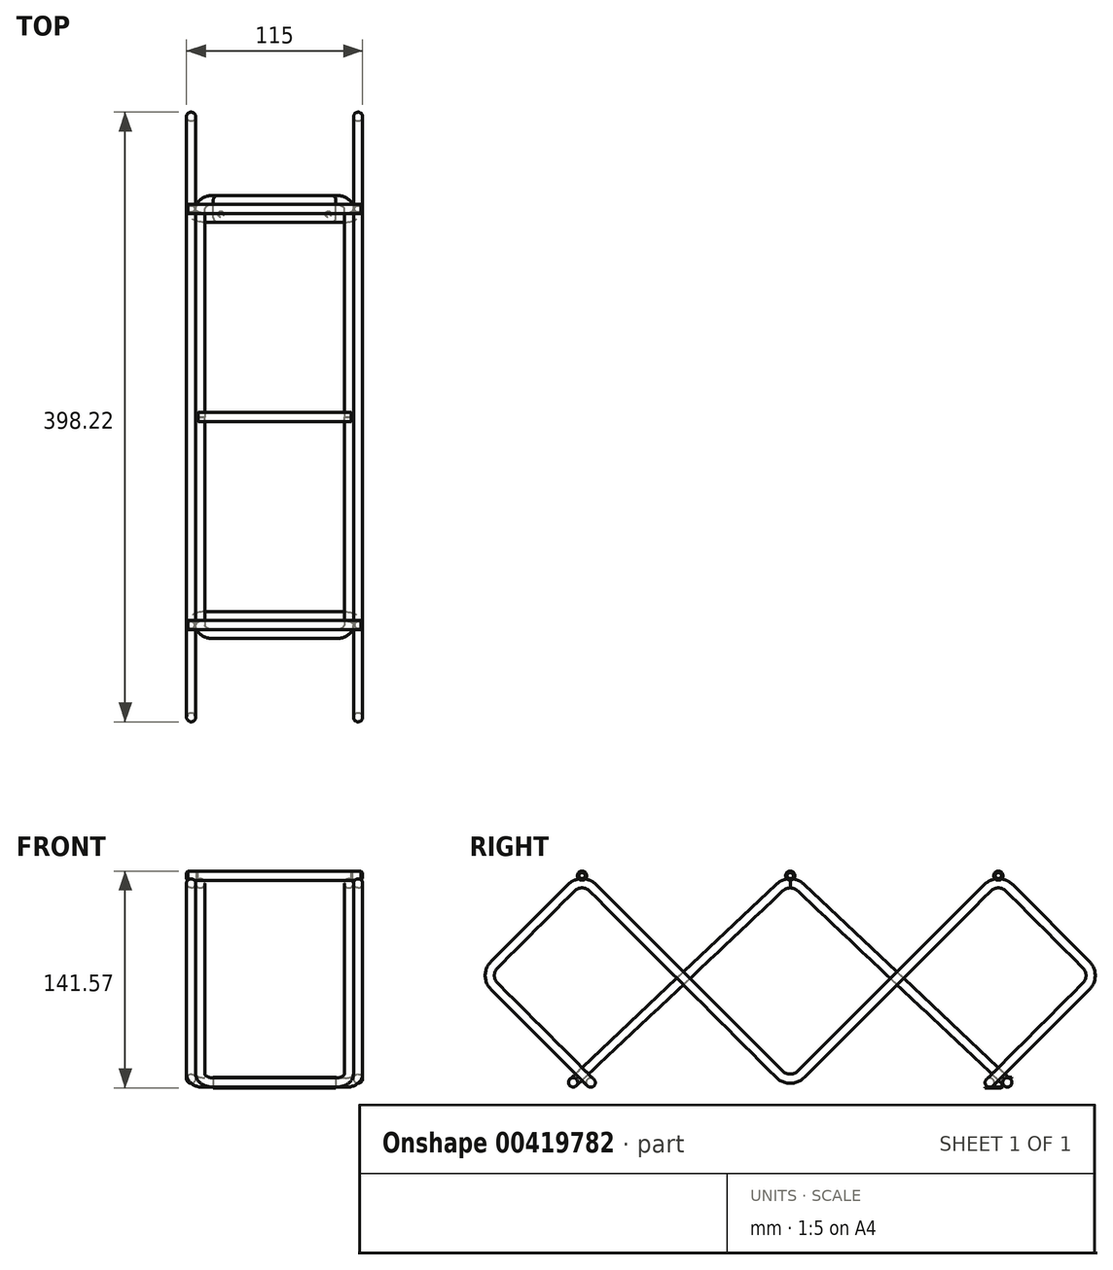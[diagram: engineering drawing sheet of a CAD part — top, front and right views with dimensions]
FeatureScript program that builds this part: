
annotation { "Feature Type Name" : "Feature", "Feature Type Description" : "" }
export const myFeature = defineFeature(function(context is Context, id is Id, definition is map)
    precondition{}
    {
        {
            var Q0;
            Q0=qCreatedBy(makeId("Right.planeOp"),FACE);
            cPlane(context, id + "F0", {"entities" : qUnion([Q0]), "cplaneType" : CPlaneType.OFFSET, "offset" : (109 / 2) * mm, "width" : 150 * mm, "height" : 150 * mm});
        }
        {
            var Q0;
            Q0=qCreatedBy(id+"F0.planeOp",FACE);
            var sketch = newSketch(context, id + "F1", { "sketchPlane" : qUnion([Q0])});
            skLineSegment(sketch, "E0", {"start": v(-7.07, 6.93) * mm, "end": v(-128.84, 128.7) * mm});
            skLineSegment(sketch, "E1", {"start": v(-142.98, 128.7) * mm, "end": v(-193.18, 78.49) * mm});
            skLineSegment(sketch, "E2", {"start": v(-193.18, 64.35) * mm, "end": v(-135.9, 7.07) * mm});
            skLineSegment(sketch, "E3", {"start": v(-135.9, 7.07) * mm, "end": v(-128.84, 0) * mm, "construction": true});
            skPoint(sketch, "E4.visualSharp", {"position": v(-135.9, 135.76) * mm});
            skArc(sketch, "E4.filletArc", {"start": v(-128.84, 128.7) * mm, "mid": v(-135.9, 131.62) * mm, "end": v(-142.98, 128.7) * mm});
            skPoint(sketch, "E5.visualSharp", {"position": v(-200.25, 71.42) * mm});
            skArc(sketch, "E5.filletArc", {"start": v(-193.18, 78.49) * mm, "mid": v(-196.11, 71.42) * mm, "end": v(-193.18, 64.35) * mm});
            skLineSegment(sketch, "E6", {"start": v(-193.18, 64.35) * mm, "end": v(-200.25, 71.42) * mm, "construction": true});
            skLineSegment(sketch, "E7", {"start": v(-128.84, 128.7) * mm, "end": v(-128.84, 0) * mm, "construction": true});
            skLineSegment(sketch, "E8", {"start": v(-128.84, 4) * mm, "end": v(0, 4) * mm, "construction": true});
            skArc(sketch, "E9", {"start": v(-7.07, 6.93) * mm, "mid": v(-3.83, 4.76) * mm, "end": v(0, 4) * mm});
            skLineSegment(sketch, "E10", {"start": v(0, 4) * mm, "end": v(7.54, 4) * mm, "construction": true});
            skLineSegment(sketch, "E11", {"start": v(-135.9, 121.62) * mm, "end": v(-135.9, 7.07) * mm, "construction": true});
            skSolve(sketch);
        }
        {
            var Q0;
            Q0=qCreatedBy(makeId("Front.planeOp"),FACE);
            var sketch = newSketch(context, id + "F2", { "sketchPlane" : qUnion([Q0])});
            skCircle(sketch, "E12", {"center": v(54.5, 4) * mm, "radius": 3 * mm});
            skSolve(sketch);
        }
        {
            var Q0;
            Q0=makeQuery(id+"F2.imprint","IMPRINT",FACE,{"disambiguationData":[TD([[makeQuery(id+"F2.imprint","IMPRINT",EDGE,{"derivedFrom":sQuery(id+"F2.wireOp",EDGE,"E12")}),1.0]])]});
            var Q1;
            Q1=sQuery(id+"F1.wireOp",EDGE,"E9");
            var Q2;
            Q2=sQuery(id+"F1.wireOp",EDGE,"E0");
            var Q3;
            Q3=sQuery(id+"F1.wireOp",EDGE,"E4.filletArc");
            var Q4;
            Q4=sQuery(id+"F1.wireOp",EDGE,"E1");
            var Q5;
            Q5=sQuery(id+"F1.wireOp",EDGE,"E5.filletArc");
            var Q6;
            Q6=sQuery(id+"F1.wireOp",EDGE,"E2");
            sweep(context, id + "F3", {"profiles" : qUnion([Q0]), "path" : qUnion([Q1, Q2, Q3, Q4, Q5, Q6])});
        }
        {
            var Q0;
            Q0=sQuery(id+"F1.wireOp",EDGE,"E3");
            var Q1;
            Q1=qCreatedBy(makeId("Right.planeOp"),FACE);
            cPlane(context, id + "F4", {"entities" : qUnion([Q0, Q1]), "cplaneType" : CPlaneType.LINE_ANGLE, "offset" : 25 * mm, "angle" : 90 * degree, "width" : 150 * mm, "height" : 150 * mm});
        }
        {
            var Q0;
            Q0=qCreatedBy(id+"F4.planeOp",FACE);
            var sketch = newSketch(context, id + "F5", { "sketchPlane" : qUnion([Q0])});
            skArc(sketch, "E13", {"start": v(-54.5, 101.1) * mm, "mid": v(-52.16, 95.44) * mm, "end": v(-46.5, 93.1) * mm});
            skLineSegment(sketch, "E14", {"start": v(-52.5, 93.1) * mm, "end": v(-46.5, 93.1) * mm, "construction": true});
            skLineSegment(sketch, "E15.0", {"start": v(-54.5, 182.1) * mm, "end": v(-54.5, 101.1) * mm, "construction": true});
            skLineSegment(sketch, "E16", {"start": v(-46.5, 93.1) * mm, "end": v(-46.5, 101.1) * mm, "construction": true});
            skLineSegment(sketch, "E17", {"start": v(-54.5, 101.1) * mm, "end": v(-46.5, 101.1) * mm, "construction": true});
            skLineSegment(sketch, "E18", {"start": v(-46.5, 93.1) * mm, "end": v(0, 93.1) * mm});
            skSolve(sketch);
        }
        {
            var Q0;
            Q0=makeQuery(id+"F3.opSweep","CAP_FACE",FACE,{"disambiguationData":[OSD([sQuery(id+"F1.wireOp",VERTEX,"E2.end"),sQuery(id+"F2.wireOp",EDGE,"E12")])],"isStart":false});
            var Q1;
            Q1=sQuery(id+"F5.wireOp",EDGE,"E13");
            var Q2;
            Q2=sQuery(id+"F5.wireOp",EDGE,"E18");
            sweep(context, id + "F6", {"operationType" : NewBodyOperationType.ADD, "profiles" : qUnion([Q0]), "path" : qUnion([Q1, Q2])});
        }
        {
            var Q0;
            Q0=makeQuery(id+"F3.opSweep","SWEPT_BODY",BODY,{"disambiguationData":[OSD([sQuery(id+"F1.wireOp",EDGE,"E2"),sQuery(id+"F2.wireOp",EDGE,"E12")])]});
            var Q1;
            Q1=makeQuery(id+"F6.opSweep","CAP_FACE",FACE,{"disambiguationData":[OSD([sQuery(id+"F1.wireOp",VERTEX,"E2.end"),sQuery(id+"F2.wireOp",EDGE,"E12"),sQuery(id+"F5.wireOp",VERTEX,"E18.end")])],"isStart":false});
            mirror(context, id + "F7", {"operationType" : NewBodyOperationType.ADD, "entities" : qUnion([Q0]), "mirrorPlane" : qUnion([Q1])});
        }
        {
            var Q0;
            Q0=qCreatedBy(makeId("Right.planeOp"),FACE);
            var sketch = newSketch(context, id + "F8", { "sketchPlane" : qUnion([Q0])});
            skCircle(sketch, "E19", {"center": v(-135.9, 136.62) * mm, "radius": 3 * mm});
            skLineSegment(sketch, "E20", {"start": v(-135.9, 136.62) * mm, "end": v(-135.9, 135.76) * mm, "construction": true});
            skSolve(sketch);
        }
        {
            var Q0;
            Q0 = qSketchRegion(id + "F8", true);
            extrude(context, id + "F9", {"entities" : qUnion([Q0]), "endBound" : BoundingType.SYMMETRIC, "offsetDistance" : 25 * mm, "depth" : 115 * mm});
        }
        {
            var Q0;
            Q0=makeQuery(id+"F3.opSweep","SWEPT_BODY",BODY,{"disambiguationData":[OSD([sQuery(id+"F1.wireOp",EDGE,"E2"),sQuery(id+"F2.wireOp",EDGE,"E12")])]});
            var Q1;
            Q1=makeQuery(id+"F3.opSweep","CAP_FACE",FACE,{"disambiguationData":[OSD([sQuery(id+"F1.wireOp",VERTEX,"u9EGyw18-Stdu-PzCn-n0PT-0w15YMYe05o3.end"),sQuery(id+"F2.wireOp",EDGE,"E12")])],"isStart":true});
            mirror(context, id + "F10", {"operationType" : NewBodyOperationType.ADD, "entities" : qUnion([Q0]), "mirrorPlane" : qUnion([Q1])});
        }
        {
            var Q0;
            Q0=makeQuery(id+"F9.opExtrude","SWEPT_BODY",BODY,{"disambiguationData":[OSD([sQuery(id+"F8.wireOp",EDGE,"E19")])]});
            var Q1;
            Q1=qCreatedBy(makeId("Front.planeOp"),FACE);
            mirror(context, id + "F11", {"entities" : qUnion([Q0]), "mirrorPlane" : qUnion([Q1])});
        }
        {
            var Q0;
            Q0=qCreatedBy(id+"F0.planeOp",FACE);
            cPlane(context, id + "F12", {"entities" : qUnion([Q0]), "cplaneType" : CPlaneType.OFFSET, "offset" : 6 * mm, "oppositeDirection" : true, "width" : 150 * mm, "height" : 150 * mm});
        }
        {
            var Q0;
            Q0=qCreatedBy(id+"F12.planeOp",FACE);
            var sketch = newSketch(context, id + "F13", { "sketchPlane" : qUnion([Q0])});
            skLineSegment(sketch, "E21", {"start": v(-135.9, 7.07) * mm, "end": v(-6.86, 128.9) * mm});
            skLineSegment(sketch, "E22", {"start": v(-135.9, 7.07) * mm, "end": v(-143.18, 0.2) * mm, "construction": true});
            skLineSegment(sketch, "E23", {"start": v(0, 0) * mm, "end": v(0, 135.76) * mm, "construction": true});
            skLineSegment(sketch, "E24", {"start": v(-135.9, 135.76) * mm, "end": v(0, 135.76) * mm, "construction": true});
            skArc(sketch, "E25", {"start": v(0, 131.62) * mm, "mid": v(-3.7, 130.92) * mm, "end": v(-6.86, 128.9) * mm});
            skLineSegment(sketch, "E26", {"start": v(-135.9, 121.62) * mm, "end": v(0, 121.62) * mm, "construction": true});
            skSolve(sketch);
        }
        {
            var Q0;
            Q0=sQuery(id+"F13.wireOp",EDGE,"E22");
            var Q1;
            Q1=qCreatedBy(id+"F12.planeOp",FACE);
            cPlane(context, id + "F14", {"entities" : qUnion([Q0, Q1]), "cplaneType" : CPlaneType.LINE_ANGLE, "offset" : 25 * mm, "angle" : 90 * degree, "width" : 150 * mm, "height" : 150 * mm});
        }
        {
            var Q0;
            Q0=qCreatedBy(id+"F14.planeOp",FACE);
            var sketch = newSketch(context, id + "F15", { "sketchPlane" : qUnion([Q0])});
            skLineSegment(sketch, "E27", {"start": v(48.5, 101.97) * mm, "end": v(40.5, 101.97) * mm, "construction": true});
            skArc(sketch, "E28", {"start": v(48.5, 93.97) * mm, "mid": v(46.16, 99.63) * mm, "end": v(40.5, 101.97) * mm});
            skLineSegment(sketch, "E29", {"start": v(40.5, 101.97) * mm, "end": v(0, 101.97) * mm});
            skLineSegment(sketch, "E30", {"start": v(48.5, 93.97) * mm, "end": v(48.5, 101.97) * mm, "construction": true});
            skSolve(sketch);
        }
        {
            var Q0;
            Q0=qCreatedBy(makeId("Front.planeOp"),FACE);
            var sketch = newSketch(context, id + "F16", { "sketchPlane" : qUnion([Q0])});
            skCircle(sketch, "E31", {"center": v(48.5, 131.62) * mm, "radius": 3 * mm});
            skSolve(sketch);
        }
        {
            var Q0;
            Q0=makeQuery(id+"F16.imprint","IMPRINT",FACE,{"disambiguationData":[TD([[makeQuery(id+"F16.imprint","IMPRINT",EDGE,{"derivedFrom":sQuery(id+"F16.wireOp",EDGE,"E31")}),1.0]])]});
            var Q1;
            Q1=sQuery(id+"F13.wireOp",EDGE,"E25");
            var Q2;
            Q2=sQuery(id+"F13.wireOp",EDGE,"E21");
            var Q3;
            Q3=sQuery(id+"F15.wireOp",EDGE,"E28");
            var Q4;
            Q4=sQuery(id+"F15.wireOp",EDGE,"E29");
            sweep(context, id + "F17", {"profiles" : qUnion([Q0]), "path" : qUnion([Q1, Q2, Q3, Q4])});
        }
        {
            var Q0;
            Q0=makeQuery(id+"F17.opSweep","SWEPT_BODY",BODY,{"disambiguationData":[OSD([sQuery(id+"F15.wireOp",EDGE,"E29"),sQuery(id+"F16.wireOp",EDGE,"E31")])]});
            var Q1;
            Q1=makeQuery(id+"F17.opSweep","CAP_FACE",FACE,{"disambiguationData":[OSD([sQuery(id+"F15.wireOp",VERTEX,"E29.end"),sQuery(id+"F16.wireOp",EDGE,"E31")])],"isStart":false});
            mirror(context, id + "F18", {"operationType" : NewBodyOperationType.ADD, "entities" : qUnion([Q0]), "mirrorPlane" : qUnion([Q1])});
        }
        {
            var Q0;
            Q0=makeQuery(id+"F17.opSweep","SWEPT_BODY",BODY,{"disambiguationData":[OSD([sQuery(id+"F15.wireOp",EDGE,"E29"),sQuery(id+"F16.wireOp",EDGE,"E31")])]});
            var Q1;
            Q1=makeQuery(id+"F18.opPattern","COPY",FACE,{"derivedFrom":makeQuery(id+"F17.opSweep","CAP_FACE",FACE,{"disambiguationData":[OSD([sQuery(id+"F13.wireOp",VERTEX,"E25.start"),sQuery(id+"F16.wireOp",EDGE,"E31")])],"isStart":true}),"instanceName":"1"});
            mirror(context, id + "F19", {"operationType" : NewBodyOperationType.ADD, "entities" : qUnion([Q0]), "mirrorPlane" : qUnion([Q1])});
        }
        {
            var Q0;
            Q0=makeQuery(id+"F9.opExtrude","CAP_FACE",FACE,{"disambiguationData":[OSD([sQuery(id+"F8.wireOp",EDGE,"E19")])],"isStart":false});
            var Q1;
            Q1=makeQuery(id+"F9.opExtrude","CAP_FACE",FACE,{"disambiguationData":[OSD([sQuery(id+"F8.wireOp",EDGE,"E19")])],"isStart":true});
            var Q2;
            Q2=makeQuery(id+"F10.opPattern","COPY",FACE,{"derivedFrom":makeQuery(id+"F9.opExtrude","CAP_FACE",FACE,{"disambiguationData":[OSD([sQuery(id+"F8.wireOp",EDGE,"E19")])],"isStart":true}),"instanceName":"1"});
            var Q3;
            Q3=makeQuery(id+"F10.opPattern","COPY",FACE,{"derivedFrom":makeQuery(id+"F9.opExtrude","CAP_FACE",FACE,{"disambiguationData":[OSD([sQuery(id+"F8.wireOp",EDGE,"E19")])],"isStart":false}),"instanceName":"1"});
            chamfer(context, id + "F20", {"entities" : qUnion([Q0, Q1, Q2, Q3]), "width" : 1 * mm, "tangentPropagation" : true});
        }
        {
            var Q0;
            Q0=qCreatedBy(makeId("Right.planeOp"),FACE);
            var sketch = newSketch(context, id + "F21", { "sketchPlane" : qUnion([Q0])});
            skCircle(sketch, "E32.0", {"center": v(130.25, 1.41) * mm, "radius": 3 * mm, "construction": true});
            skCircle(sketch, "E32.1", {"center": v(141.72, 1.58) * mm, "radius": 3 * mm, "construction": true});
            skLineSegment(sketch, "E33", {"start": v(132.8, 3.58) * mm, "end": v(132.8, 2.98) * mm});
            skLineSegment(sketch, "E34", {"start": v(127.25, -1.59) * mm, "end": v(138.32, -1.59) * mm});
            skArc(sketch, "E35", {"start": v(141.72, 4.98) * mm, "mid": v(139.32, 3.98) * mm, "end": v(138.32, 1.58) * mm});
            skLineSegment(sketch, "E36", {"start": v(141.72, 4.98) * mm, "end": v(144.72, 4.98) * mm});
            skLineSegment(sketch, "E37", {"start": v(138.32, 1.58) * mm, "end": v(138.32, -1.59) * mm});
            skLineSegment(sketch, "E38.0", {"start": v(141.72, 4.62) * mm, "end": v(144.72, 4.62) * mm});
            skArc(sketch, "E38.1", {"start": v(141.72, 4.62) * mm, "mid": v(139.57, 3.73) * mm, "end": v(138.68, 1.58) * mm});
            skLineSegment(sketch, "E38.2", {"start": v(138.68, 1.58) * mm, "end": v(138.68, -1.95) * mm});
            skLineSegment(sketch, "E38.3", {"start": v(127.25, -1.95) * mm, "end": v(138.68, -1.95) * mm});
            skLineSegment(sketch, "E39", {"start": v(127.25, -1.95) * mm, "end": v(127.25, -1.59) * mm});
            skLineSegment(sketch, "E40", {"start": v(144.72, 4.62) * mm, "end": v(144.72, 4.98) * mm});
            skLineSegment(sketch, "E41", {"start": v(127.25, -1.59) * mm, "end": v(127.25, 1.41) * mm});
            skLineSegment(sketch, "E42", {"start": v(144.72, 1.58) * mm, "end": v(144.72, 4.62) * mm, "construction": true});
            skSolve(sketch);
        }
        {
            var Q0;
            Q0 = qSketchRegion(id + "F21", true);
            extrude(context, id + "F22", {"entities" : qUnion([Q0]), "endBound" : BoundingType.SYMMETRIC, "offsetDistance" : 25 * mm, "depth" : 80 * mm});
        }
        {
            var Q0;
            Q0=qCreatedBy(makeId("Right.planeOp"),FACE);
            var sketch = newSketch(context, id + "F23", { "sketchPlane" : qUnion([Q0])});
            skCircle(sketch, "E43", {"center": v(0, 136.62) * mm, "radius": 3 * mm});
            skArc(sketch, "E44.0", {"start": v(141.55, 134.11) * mm, "mid": v(139.9, 139.62) * mm, "end": v(138.26, 134.11) * mm, "construction": true});
            skLineSegment(sketch, "E45", {"start": v(139.9, 136.62) * mm, "end": v(0, 136.62) * mm, "construction": true});
            skSolve(sketch);
        }
        {
            var Q0;
            Q0 = qSketchRegion(id + "F23", true);
            extrude(context, id + "F24", {"entities" : qUnion([Q0]), "endBound" : BoundingType.SYMMETRIC, "offsetDistance" : 25 * mm, "depth" : 102 * mm});
        }
        {
            var Q0;
            Q0=makeQuery(id+"F24.opExtrude","CAP_EDGE",EDGE,{"disambiguationData":[OSD([sQuery(id+"F23.wireOp",EDGE,"E43")])],"isStart":true});
            var Q1;
            Q1=makeQuery(id+"F24.opExtrude","CAP_FACE",FACE,{"disambiguationData":[OSD([sQuery(id+"F23.wireOp",EDGE,"E43")])],"isStart":false});
            chamfer(context, id + "F25", {"entities" : qUnion([Q0, Q1]), "width" : 1 * mm, "tangentPropagation" : true});
        }
        {
            var Q0;
            Q0=makeQuery(id+"F22.opExtrude","CAP_EDGE",EDGE,{"disambiguationData":[OSD([sQuery(id+"F21.wireOp",EDGE,"E40")])],"isStart":true});
            var Q1;
            Q1=makeQuery(id+"F22.opExtrude","CAP_EDGE",EDGE,{"disambiguationData":[OSD([sQuery(id+"F21.wireOp",EDGE,"E39")])],"isStart":true});
            var Q2;
            Q2=makeQuery(id+"F22.opExtrude","CAP_EDGE",EDGE,{"disambiguationData":[OSD([sQuery(id+"F21.wireOp",EDGE,"E39")])],"isStart":false});
            var Q3;
            Q3=makeQuery(id+"F22.opExtrude","CAP_EDGE",EDGE,{"disambiguationData":[OSD([sQuery(id+"F21.wireOp",EDGE,"E40")])],"isStart":false});
            fillet(context, id + "F26", {"entities" : qUnion([Q0, Q1, Q2, Q3]), "radius" : 3 * mm, "tangentPropagation" : true, "allowEdgeOverflow" : false});
        }
        {
            var Q0;
            Q0=makeQuery(id+"F22.opExtrude","SWEPT_EDGE",EDGE,{"disambiguationData":[OSD([sQuery(id+"F21.wireOp",EDGE,"E34"),sQuery(id+"F21.wireOp",EDGE,"E37")])]});
            var Q1;
            Q1=makeQuery(id+"F22.opExtrude","SWEPT_EDGE",EDGE,{"disambiguationData":[OSD([sQuery(id+"F21.wireOp",EDGE,"E38.2"),sQuery(id+"F21.wireOp",EDGE,"E38.3")])]});
            fillet(context, id + "F27", {"entities" : qUnion([Q0, Q1]), "radius" : 1 * mm, "tangentPropagation" : true, "allowEdgeOverflow" : false});
        }
        {
            var Q0;
            Q0=makeQuery(id+"F22.opExtrude","SWEPT_FACE",FACE,{"disambiguationData":[OSD([sQuery(id+"F21.wireOp",EDGE,"E34")])]});
            var sketch = newSketch(context, id + "F28", { "sketchPlane" : qUnion([Q0])});
            skPoint(sketch, "E46", {"position": v(-35, 132.25) * mm});
            skPoint(sketch, "E47", {"position": v(35, 132.25) * mm});
            skLineSegment(sketch, "E48", {"start": v(0, 132.25) * mm, "end": v(-35, 132.25) * mm, "construction": true});
            skPoint(sketch, "E48.startSnap0", {"position": v(0, 127.25) * mm});
            skLineSegment(sketch, "E49", {"start": v(-35, 132.25) * mm, "end": v(-40, 132.25) * mm, "construction": true});
            skLineSegment(sketch, "E50", {"start": v(-35, 132.25) * mm, "end": v(-35, 127.25) * mm, "construction": true});
            skLineSegment(sketch, "E51", {"start": v(0, 132.25) * mm, "end": v(35, 132.25) * mm, "construction": true});
            skSolve(sketch);
        }
        {
            var Q0;
            Q0=sQuery(id+"F28.wireOp",VERTEX,"E47");
            var Q1;
            Q1=sQuery(id+"F28.wireOp",VERTEX,"E46");
            var Q2;
            Q2=makeQuery(id+"F22.opExtrude","SWEPT_BODY",BODY,{"disambiguationData":[OSD([sQuery(id+"F21.wireOp",EDGE,"E34"),sQuery(id+"F21.wireOp",EDGE,"E35"),sQuery(id+"F21.wireOp",EDGE,"E36"),sQuery(id+"F21.wireOp",EDGE,"E37"),sQuery(id+"F21.wireOp",EDGE,"E38.0"),sQuery(id+"F21.wireOp",EDGE,"E38.1"),sQuery(id+"F21.wireOp",EDGE,"E38.2"),sQuery(id+"F21.wireOp",EDGE,"E38.3"),sQuery(id+"F21.wireOp",EDGE,"E39"),sQuery(id+"F21.wireOp",EDGE,"E40")])]});
            hole(context, id + "F29", {"style" : HoleStyle.C_SINK, "endStyle" : HoleEndStyle.BLIND, "holeDiameter" : 2 * mm, "cSinkDiameter" : 4 * mm, "cSinkAngle" : 90 * degree, "holeDepth" : 5 * mm, "isTappedThrough" : true, "tappedDepth" : 12 * mm, "tapClearance" : 3, "locations" : qUnion([Q0, Q1]), "scope" : qUnion([Q2])});
        }
        {
            var Q0;
            Q0=makeQuery(id+"F11.opPattern","COPY",EDGE,{"derivedFrom":makeQuery(id+"F9.opExtrude","CAP_EDGE",EDGE,{"disambiguationData":[OSD([sQuery(id+"F8.wireOp",EDGE,"E19")])],"isStart":true}),"instanceName":"1"});
            var Q1;
            Q1=makeQuery(id+"F11.opPattern","COPY",EDGE,{"derivedFrom":makeQuery(id+"F9.opExtrude","CAP_EDGE",EDGE,{"disambiguationData":[OSD([sQuery(id+"F8.wireOp",EDGE,"E19")])],"isStart":false}),"instanceName":"1"});
            chamfer(context, id + "F30", {"entities" : qUnion([Q0, Q1]), "width" : 1 * mm, "tangentPropagation" : true});
        }
    });
